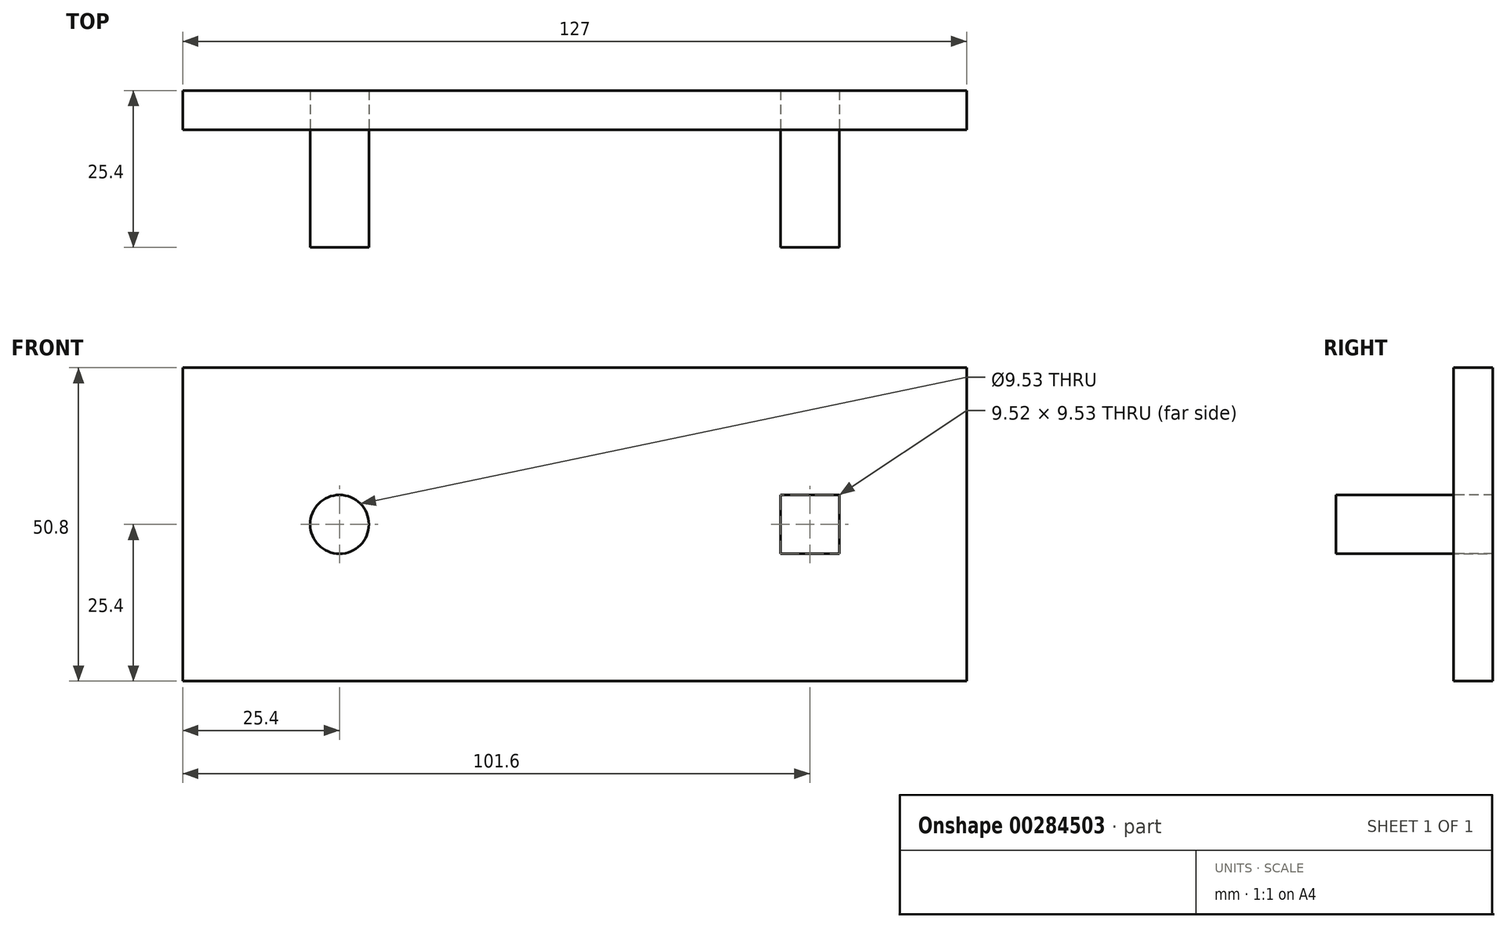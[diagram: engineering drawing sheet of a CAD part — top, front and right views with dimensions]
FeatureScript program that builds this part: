
annotation { "Feature Type Name" : "Feature", "Feature Type Description" : "" }
export const myFeature = defineFeature(function(context is Context, id is Id, definition is map)
    precondition{}
    {
        {
            var Q0;
            Q0=qCreatedBy(makeId("Front.planeOp"),FACE);
            var sketch = newSketch(context, id + "F0", { "sketchPlane" : qUnion([Q0])});
            skLineSegment(sketch, "E0.bottom", {"start": v(-63.5, 25.4) * mm, "end": v(63.5, 25.4) * mm});
            skLineSegment(sketch, "E0.top", {"start": v(-63.5, -25.4) * mm, "end": v(63.5, -25.4) * mm});
            skLineSegment(sketch, "E0.left", {"start": v(-63.5, 25.4) * mm, "end": v(-63.5, -25.4) * mm});
            skLineSegment(sketch, "E0.right", {"start": v(63.5, 25.4) * mm, "end": v(63.5, -25.4) * mm});
            skPoint(sketch, "E0.middle", {"position": v(0, 0) * mm});
            skLineSegment(sketch, "E1", {"start": v(-63.5, 0) * mm, "end": v(-38.1, 0) * mm});
            skPoint(sketch, "E1.endSnap0", {"position": v(-63.5, 0) * mm});
            skLineSegment(sketch, "E2", {"start": v(63.5, 0) * mm, "end": v(38.1, 0) * mm});
            skPoint(sketch, "E2.endSnap0", {"position": v(63.5, 0) * mm});
            skCircle(sketch, "E3", {"center": v(-38.1, 0) * mm, "radius": 4.76 * mm});
            skLineSegment(sketch, "E4.bottom", {"start": v(33.34, 4.76) * mm, "end": v(42.86, 4.76) * mm});
            skLineSegment(sketch, "E4.top", {"start": v(33.34, -4.76) * mm, "end": v(42.86, -4.76) * mm});
            skLineSegment(sketch, "E4.left", {"start": v(33.34, 4.76) * mm, "end": v(33.34, -4.76) * mm});
            skLineSegment(sketch, "E4.right", {"start": v(42.86, 4.76) * mm, "end": v(42.86, -4.76) * mm});
            skPoint(sketch, "E4.middle", {"position": v(38.1, 0) * mm});
            skSolve(sketch);
        }
        {
            var Q0;
            {var subQ1=sQuery(id+"F0.wireOp",EDGE,"E4.bottom");Q0=makeQuery(id+"F0.imprint","IMPRINT",FACE,{"disambiguationData":[TD([[makeQuery(id+"F0.imprint","IMPRINT",EDGE,{"derivedFrom":subQ1}),-1.0]])]});}
            var Q1;
            Q1=makeQuery(id+"F0.imprint","IMPRINT",FACE,{"disambiguationData":[TD([[makeQuery(id+"F0.imprint","IMPRINT",EDGE,{"derivedFrom":sQuery(id+"F0.wireOp",EDGE,"E3")}),1.0]])]});
            extrude(context, id + "F1", {"entities" : qUnion([Q0, Q1]), "depth" : 19.05 * mm, "hasSecondDirection" : true, "secondDirectionOppositeDirection" : true, "secondDirectionDepth" : 6.35 * mm});
        }
        {
            var Q0;
            {var subQ5=sQuery(id+"F0.wireOp",EDGE,"E0.bottom");Q0=makeQuery(id+"F0.imprint","IMPRINT",FACE,{"disambiguationData":[TD([[makeQuery(id+"F0.imprint","IMPRINT",EDGE,{"derivedFrom":subQ5}),-1.0]])]});}
            extrude(context, id + "F2", {"entities" : qUnion([Q0]), "oppositeDirection" : true, "depth" : 6.35 * mm});
        }
    });
